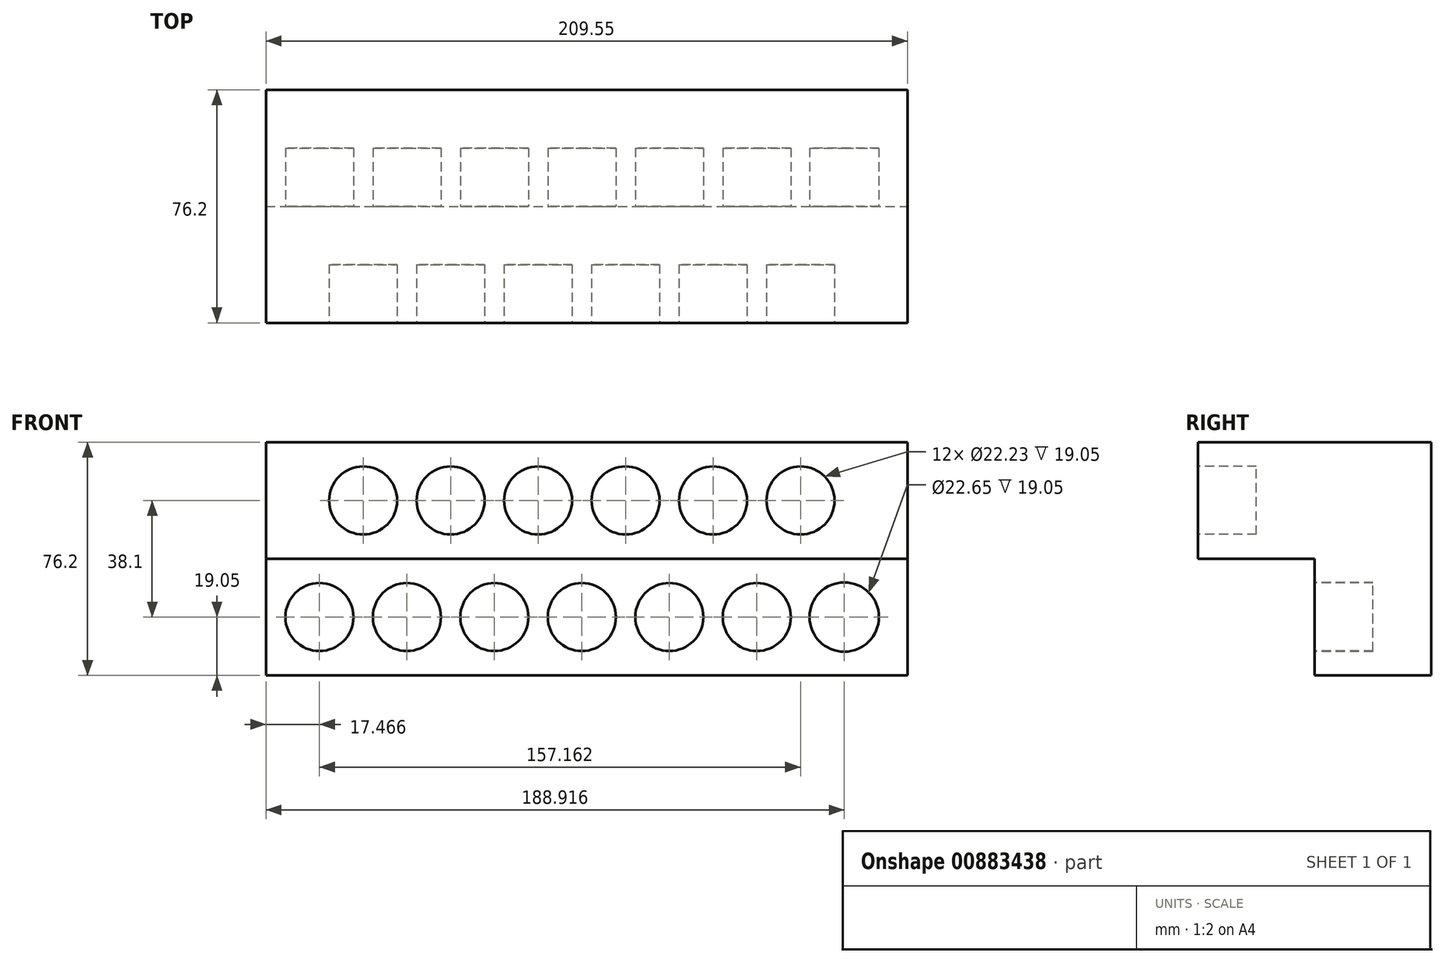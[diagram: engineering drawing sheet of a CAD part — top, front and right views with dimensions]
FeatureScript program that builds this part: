
annotation { "Feature Type Name" : "Feature", "Feature Type Description" : "" }
export const myFeature = defineFeature(function(context is Context, id is Id, definition is map)
    precondition{}
    {
        {
            var Q0;
            Q0=qCreatedBy(makeId("Front.planeOp"),FACE);
            var sketch = newSketch(context, id + "F0", { "sketchPlane" : qUnion([Q0])});
            skLineSegment(sketch, "E0.bottom", {"start": v(-74.32, 0) * mm, "end": v(135.23, 0) * mm});
            skLineSegment(sketch, "E0.top", {"start": v(-74.32, 76.2) * mm, "end": v(135.23, 76.2) * mm});
            skLineSegment(sketch, "E0.left", {"start": v(-74.32, 0) * mm, "end": v(-74.32, 76.2) * mm});
            skLineSegment(sketch, "E0.right", {"start": v(135.23, 0) * mm, "end": v(135.23, 76.2) * mm});
            skSolve(sketch);
        }
        {
            var Q0;
            Q0=makeQuery(id+"F0.imprint","IMPRINT",FACE,{"disambiguationData":[TD([[makeQuery(id+"F0.imprint","IMPRINT",EDGE,{"derivedFrom":sQuery(id+"F0.wireOp",EDGE,"E0.bottom")}),1.0]])]});
            extrude(context, id + "F1", {"entities" : qUnion([Q0]), "depth" : 76.2 * mm, "offsetDistance" : 25.4 * mm});
        }
        {
            var Q0;
            Q0=makeQuery(id+"F1.opExtrude","CAP_FACE",FACE,{"disambiguationData":[OSD([sQuery(id+"F0.wireOp",EDGE,"E0.bottom"),sQuery(id+"F0.wireOp",EDGE,"E0.top"),sQuery(id+"F0.wireOp",EDGE,"E0.left"),sQuery(id+"F0.wireOp",EDGE,"E0.right")])],"isStart":false});
            var sketch = newSketch(context, id + "F2", { "sketchPlane" : qUnion([Q0])});
            skLineSegment(sketch, "E1", {"start": v(-74.32, 38.1) * mm, "end": v(135.23, 38.1) * mm});
            skSolve(sketch);
        }
        {
            var Q0;
            {var subQ0=sQuery(id+"F2.wireOp",EDGE,"E1");Q0=makeQuery(id+"F2.imprint","IMPRINT",FACE,{"disambiguationData":[TD([[makeQuery(id+"F2.imprint","IMPRINT",EDGE,{"derivedFrom":subQ0}),-1.0]])]});}
            extrude(context, id + "F3", {"entities" : qUnion([Q0]), "operationType" : NewBodyOperationType.REMOVE, "oppositeDirection" : true, "depth" : 38.1 * mm, "offsetDistance" : 25.4 * mm});
        }
        {
            var Q0;
            Q0=makeQuery(id+"F3.boolean.opBoolean","COPY",FACE,{"derivedFrom":makeQuery(id+"F3.opExtrude","CAP_FACE",FACE,{"disambiguationData":[OSD([sQuery(id+"F0.wireOp",EDGE,"E0.bottom"),sQuery(id+"F0.wireOp",EDGE,"E0.left"),sQuery(id+"F0.wireOp",EDGE,"E0.right"),sQuery(id+"F2.wireOp",EDGE,"E1")])],"isStart":false})});
            var sketch = newSketch(context, id + "F4", { "sketchPlane" : qUnion([Q0])});
            skCircle(sketch, "E2", {"center": v(-56.85, 19.05) * mm, "radius": 11.11 * mm});
            skPoint(sketch, "E2.centerSnap0", {"position": v(-74.32, 19.05) * mm});
            skCircle(sketch, "E3", {"center": v(-28.28, 19.05) * mm, "radius": 11.11 * mm});
            skCircle(sketch, "E4", {"center": v(0.3, 19.05) * mm, "radius": 11.11 * mm});
            skCircle(sketch, "E5", {"center": v(28.87, 19.05) * mm, "radius": 11.11 * mm});
            skCircle(sketch, "E6", {"center": v(57.45, 19.05) * mm, "radius": 11.11 * mm});
            skCircle(sketch, "E7", {"center": v(86.02, 19.05) * mm, "radius": 11.11 * mm});
            skCircle(sketch, "E8", {"center": v(114.6, 19.05) * mm, "radius": 11.33 * mm});
            skSolve(sketch);
        }
        {
            var Q0;
            Q0=makeQuery(id+"F4.imprint","IMPRINT",FACE,{"disambiguationData":[TD([[makeQuery(id+"F4.imprint","IMPRINT",EDGE,{"derivedFrom":sQuery(id+"F4.wireOp",EDGE,"E2")}),1.0]])]});
            var Q1;
            Q1=makeQuery(id+"F4.imprint","IMPRINT",FACE,{"disambiguationData":[TD([[makeQuery(id+"F4.imprint","IMPRINT",EDGE,{"derivedFrom":sQuery(id+"F4.wireOp",EDGE,"E3")}),1.0]])]});
            var Q2;
            Q2=makeQuery(id+"F4.imprint","IMPRINT",FACE,{"disambiguationData":[TD([[makeQuery(id+"F4.imprint","IMPRINT",EDGE,{"derivedFrom":sQuery(id+"F4.wireOp",EDGE,"E4")}),1.0]])]});
            var Q3;
            Q3=makeQuery(id+"F4.imprint","IMPRINT",FACE,{"disambiguationData":[TD([[makeQuery(id+"F4.imprint","IMPRINT",EDGE,{"derivedFrom":sQuery(id+"F4.wireOp",EDGE,"E6")}),1.0]])]});
            var Q4;
            Q4=makeQuery(id+"F4.imprint","IMPRINT",FACE,{"disambiguationData":[TD([[makeQuery(id+"F4.imprint","IMPRINT",EDGE,{"derivedFrom":sQuery(id+"F4.wireOp",EDGE,"E7")}),1.0]])]});
            var Q5;
            Q5=makeQuery(id+"F4.imprint","IMPRINT",FACE,{"disambiguationData":[TD([[makeQuery(id+"F4.imprint","IMPRINT",EDGE,{"derivedFrom":sQuery(id+"F4.wireOp",EDGE,"E8")}),1.0]])]});
            var Q6;
            Q6=makeQuery(id+"F4.imprint","IMPRINT",FACE,{"disambiguationData":[TD([[makeQuery(id+"F4.imprint","IMPRINT",EDGE,{"derivedFrom":sQuery(id+"F4.wireOp",EDGE,"E5")}),1.0]])]});
            extrude(context, id + "F5", {"entities" : qUnion([Q0, Q1, Q2, Q3, Q4, Q5, Q6]), "operationType" : NewBodyOperationType.REMOVE, "oppositeDirection" : true, "depth" : 19.05 * mm, "offsetDistance" : 25.4 * mm});
        }
        {
            var Q0;
            Q0=makeQuery(id+"F1.opExtrude","CAP_FACE",FACE,{"disambiguationData":[OSD([sQuery(id+"F0.wireOp",EDGE,"E0.bottom"),sQuery(id+"F0.wireOp",EDGE,"E0.top"),sQuery(id+"F0.wireOp",EDGE,"E0.left"),sQuery(id+"F0.wireOp",EDGE,"E0.right")])],"isStart":false});
            var sketch = newSketch(context, id + "F6", { "sketchPlane" : qUnion([Q0])});
            skCircle(sketch, "E9", {"center": v(-42.57, 57.15) * mm, "radius": 11.11 * mm});
            skPoint(sketch, "E9.centerSnap0", {"position": v(-74.32, 57.15) * mm});
            skCircle(sketch, "E10", {"center": v(-14, 57.15) * mm, "radius": 11.11 * mm});
            skCircle(sketch, "E11", {"center": v(14.58, 57.15) * mm, "radius": 11.11 * mm});
            skCircle(sketch, "E12", {"center": v(43.16, 57.15) * mm, "radius": 11.11 * mm});
            skCircle(sketch, "E13", {"center": v(71.73, 57.15) * mm, "radius": 11.11 * mm});
            skCircle(sketch, "E14", {"center": v(100.3, 57.15) * mm, "radius": 11.11 * mm});
            skSolve(sketch);
        }
        {
            var Q0;
            Q0=makeQuery(id+"F6.imprint","IMPRINT",FACE,{"disambiguationData":[TD([[makeQuery(id+"F6.imprint","IMPRINT",EDGE,{"derivedFrom":sQuery(id+"F6.wireOp",EDGE,"E9")}),1.0]])]});
            var Q1;
            Q1=makeQuery(id+"F6.imprint","IMPRINT",FACE,{"disambiguationData":[TD([[makeQuery(id+"F6.imprint","IMPRINT",EDGE,{"derivedFrom":sQuery(id+"F6.wireOp",EDGE,"E10")}),1.0]])]});
            var Q2;
            Q2=makeQuery(id+"F6.imprint","IMPRINT",FACE,{"disambiguationData":[TD([[makeQuery(id+"F6.imprint","IMPRINT",EDGE,{"derivedFrom":sQuery(id+"F6.wireOp",EDGE,"E11")}),1.0]])]});
            var Q3;
            Q3=makeQuery(id+"F6.imprint","IMPRINT",FACE,{"disambiguationData":[TD([[makeQuery(id+"F6.imprint","IMPRINT",EDGE,{"derivedFrom":sQuery(id+"F6.wireOp",EDGE,"E12")}),1.0]])]});
            var Q4;
            Q4=makeQuery(id+"F6.imprint","IMPRINT",FACE,{"disambiguationData":[TD([[makeQuery(id+"F6.imprint","IMPRINT",EDGE,{"derivedFrom":sQuery(id+"F6.wireOp",EDGE,"E13")}),1.0]])]});
            var Q5;
            Q5=makeQuery(id+"F6.imprint","IMPRINT",FACE,{"disambiguationData":[TD([[makeQuery(id+"F6.imprint","IMPRINT",EDGE,{"derivedFrom":sQuery(id+"F6.wireOp",EDGE,"E14")}),1.0]])]});
            extrude(context, id + "F7", {"entities" : qUnion([Q0, Q1, Q2, Q3, Q4, Q5]), "operationType" : NewBodyOperationType.REMOVE, "oppositeDirection" : true, "depth" : 19.05 * mm, "offsetDistance" : 25.4 * mm});
        }
    });
